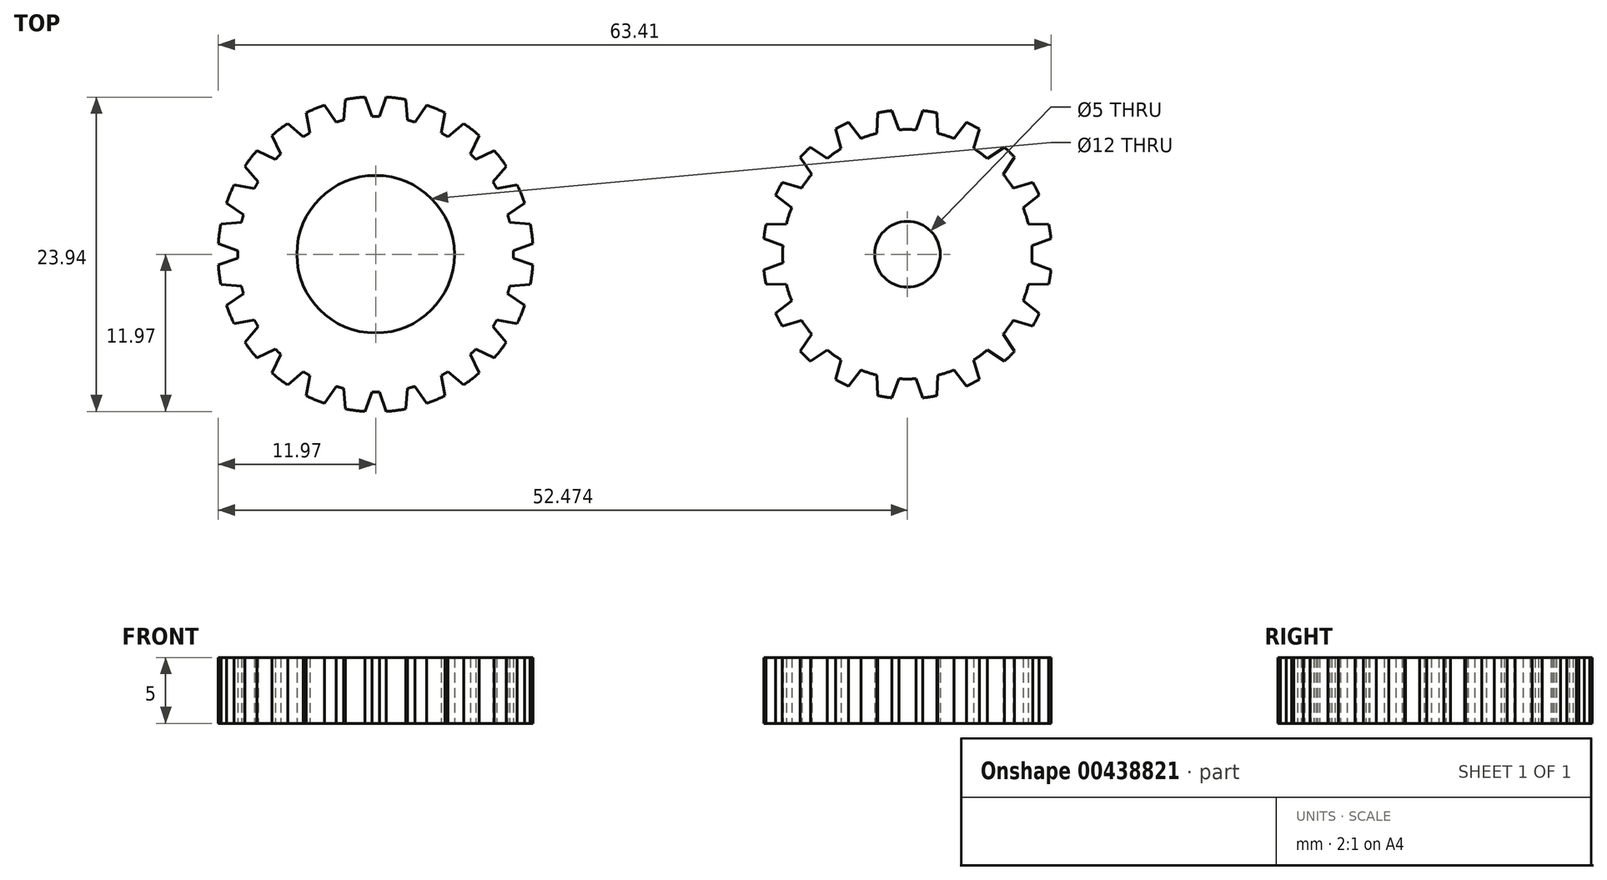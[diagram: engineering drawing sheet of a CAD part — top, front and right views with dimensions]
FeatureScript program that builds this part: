
annotation { "Feature Type Name" : "Feature", "Feature Type Description" : "" }
export const myFeature = defineFeature(function(context is Context, id is Id, definition is map)
    precondition{}
    {
        {
            var Q0;
            Q0=qCreatedBy(makeId("Top.planeOp"),FACE);
            var sketch = newSketch(context, id + "F0", { "sketchPlane" : qUnion([Q0])});
            skCircle(sketch, "E0", {"center": v(0, 0) * mm, "radius": 12 * mm});
            skCircle(sketch, "E1", {"center": v(0, 0) * mm, "radius": 6 * mm});
            skSolve(sketch);
        }
        {
            var Q0;
            Q0 = qSketchRegion(id + "F0", true);
            extrude(context, id + "F1", {"entities" : qUnion([Q0]), "depth" : 5 * mm});
        }
        {
            var Q0;
            Q0=qCreatedBy(makeId("Top.planeOp"),FACE);
            var sketch = newSketch(context, id + "F2", { "sketchPlane" : qUnion([Q0])});
            skArc(sketch, "E2", {"start": v(0.29, 10.5) * mm, "mid": v(0, 10.5) * mm, "end": v(-0.29, 10.5) * mm});
            skLineSegment(sketch, "E3", {"start": v(0.29, 10.5) * mm, "end": v(1.18, 12.95) * mm});
            skLineSegment(sketch, "E4.MirrorCS", {"start": v(-0.29, 10.5) * mm, "end": v(-1.18, 12.95) * mm});
            skLineSegment(sketch, "E5.1.0", {"start": v(-3, 10.06) * mm, "end": v(-4.49, 12.2) * mm});
            skArc(sketch, "E5.1.2", {"start": v(-2.44, 10.21) * mm, "mid": v(-2.72, 10.14) * mm, "end": v(-3, 10.06) * mm});
            skLineSegment(sketch, "E5.1.3", {"start": v(-2.44, 10.21) * mm, "end": v(-2.21, 12.81) * mm});
            skLineSegment(sketch, "E5.2.0", {"start": v(-5.5, 8.95) * mm, "end": v(-7.5, 10.62) * mm});
            skArc(sketch, "E5.2.2", {"start": v(-5, 9.23) * mm, "mid": v(-5.25, 9.1) * mm, "end": v(-5.5, 8.95) * mm});
            skLineSegment(sketch, "E5.2.3", {"start": v(-5, 9.23) * mm, "end": v(-5.45, 11.8) * mm});
            skLineSegment(sketch, "E5.3.0", {"start": v(-7.62, 7.22) * mm, "end": v(-9.99, 8.32) * mm});
            skArc(sketch, "E5.3.2", {"start": v(-7.22, 7.62) * mm, "mid": v(-7.42, 7.42) * mm, "end": v(-7.62, 7.22) * mm});
            skLineSegment(sketch, "E5.3.3", {"start": v(-7.22, 7.62) * mm, "end": v(-8.32, 9.99) * mm});
            skLineSegment(sketch, "E5.4.0", {"start": v(-9.23, 5) * mm, "end": v(-11.8, 5.45) * mm});
            skArc(sketch, "E5.4.2", {"start": v(-8.95, 5.5) * mm, "mid": v(-9.1, 5.25) * mm, "end": v(-9.23, 5) * mm});
            skLineSegment(sketch, "E5.4.3", {"start": v(-8.95, 5.5) * mm, "end": v(-10.62, 7.5) * mm});
            skLineSegment(sketch, "E5.5.0", {"start": v(-10.21, 2.44) * mm, "end": v(-12.81, 2.21) * mm});
            skArc(sketch, "E5.5.2", {"start": v(-10.06, 3) * mm, "mid": v(-10.14, 2.72) * mm, "end": v(-10.21, 2.44) * mm});
            skLineSegment(sketch, "E5.5.3", {"start": v(-10.06, 3) * mm, "end": v(-12.2, 4.49) * mm});
            skLineSegment(sketch, "E5.6.0", {"start": v(-10.5, -0.29) * mm, "end": v(-12.95, -1.18) * mm});
            skArc(sketch, "E5.6.2", {"start": v(-10.5, 0.29) * mm, "mid": v(-10.5, 0) * mm, "end": v(-10.5, -0.29) * mm});
            skLineSegment(sketch, "E5.6.3", {"start": v(-10.5, 0.29) * mm, "end": v(-12.95, 1.18) * mm});
            skLineSegment(sketch, "E5.7.0", {"start": v(-10.06, -3) * mm, "end": v(-12.2, -4.49) * mm});
            skArc(sketch, "E5.7.2", {"start": v(-10.21, -2.44) * mm, "mid": v(-10.14, -2.72) * mm, "end": v(-10.06, -3) * mm});
            skLineSegment(sketch, "E5.7.3", {"start": v(-10.21, -2.44) * mm, "end": v(-12.81, -2.21) * mm});
            skLineSegment(sketch, "E5.8.0", {"start": v(-8.95, -5.5) * mm, "end": v(-10.62, -7.5) * mm});
            skArc(sketch, "E5.8.2", {"start": v(-9.23, -5) * mm, "mid": v(-9.1, -5.25) * mm, "end": v(-8.95, -5.5) * mm});
            skLineSegment(sketch, "E5.8.3", {"start": v(-9.23, -5) * mm, "end": v(-11.8, -5.45) * mm});
            skLineSegment(sketch, "E5.9.0", {"start": v(-7.22, -7.62) * mm, "end": v(-8.32, -9.99) * mm});
            skArc(sketch, "E5.9.2", {"start": v(-7.62, -7.22) * mm, "mid": v(-7.42, -7.42) * mm, "end": v(-7.22, -7.62) * mm});
            skLineSegment(sketch, "E5.9.3", {"start": v(-7.62, -7.22) * mm, "end": v(-9.99, -8.32) * mm});
            skLineSegment(sketch, "E6.1.10.0", {"start": v(-5, -9.23) * mm, "end": v(-5.45, -11.8) * mm});
            skArc(sketch, "E6.7.10.0", {"start": v(-5.5, -8.95) * mm, "mid": v(-5.25, -9.1) * mm, "end": v(-5, -9.23) * mm});
            skLineSegment(sketch, "E6.11.10.0", {"start": v(-5.5, -8.95) * mm, "end": v(-7.5, -10.62) * mm});
            skLineSegment(sketch, "E6.1.11.0", {"start": v(-2.44, -10.21) * mm, "end": v(-2.21, -12.81) * mm});
            skArc(sketch, "E6.7.11.0", {"start": v(-3, -10.06) * mm, "mid": v(-2.72, -10.14) * mm, "end": v(-2.44, -10.21) * mm});
            skLineSegment(sketch, "E6.11.11.0", {"start": v(-3, -10.06) * mm, "end": v(-4.49, -12.2) * mm});
            skLineSegment(sketch, "E6.1.12.0", {"start": v(0.29, -10.5) * mm, "end": v(1.18, -12.95) * mm});
            skArc(sketch, "E6.7.12.0", {"start": v(-0.29, -10.5) * mm, "mid": v(0, -10.5) * mm, "end": v(0.29, -10.5) * mm});
            skLineSegment(sketch, "E6.11.12.0", {"start": v(-0.29, -10.5) * mm, "end": v(-1.18, -12.95) * mm});
            skLineSegment(sketch, "E6.1.13.0", {"start": v(3, -10.06) * mm, "end": v(4.49, -12.2) * mm});
            skArc(sketch, "E6.7.13.0", {"start": v(2.44, -10.21) * mm, "mid": v(2.72, -10.14) * mm, "end": v(3, -10.06) * mm});
            skLineSegment(sketch, "E6.11.13.0", {"start": v(2.44, -10.21) * mm, "end": v(2.21, -12.81) * mm});
            skLineSegment(sketch, "E7.1.14.0", {"start": v(5.5, -8.95) * mm, "end": v(7.5, -10.62) * mm});
            skArc(sketch, "E7.7.14.0", {"start": v(5, -9.23) * mm, "mid": v(5.25, -9.1) * mm, "end": v(5.5, -8.95) * mm});
            skLineSegment(sketch, "E7.11.14.0", {"start": v(5, -9.23) * mm, "end": v(5.45, -11.8) * mm});
            skLineSegment(sketch, "E7.1.15.0", {"start": v(7.62, -7.22) * mm, "end": v(9.99, -8.32) * mm});
            skArc(sketch, "E7.7.15.0", {"start": v(7.22, -7.62) * mm, "mid": v(7.42, -7.42) * mm, "end": v(7.62, -7.22) * mm});
            skLineSegment(sketch, "E7.11.15.0", {"start": v(7.22, -7.62) * mm, "end": v(8.32, -9.99) * mm});
            skLineSegment(sketch, "E7.1.16.0", {"start": v(9.23, -5) * mm, "end": v(11.8, -5.45) * mm});
            skArc(sketch, "E7.7.16.0", {"start": v(8.95, -5.5) * mm, "mid": v(9.1, -5.25) * mm, "end": v(9.23, -5) * mm});
            skLineSegment(sketch, "E7.11.16.0", {"start": v(8.95, -5.5) * mm, "end": v(10.62, -7.5) * mm});
            skLineSegment(sketch, "E7.1.17.0", {"start": v(10.21, -2.44) * mm, "end": v(12.81, -2.21) * mm});
            skArc(sketch, "E7.7.17.0", {"start": v(10.06, -3) * mm, "mid": v(10.14, -2.72) * mm, "end": v(10.21, -2.44) * mm});
            skLineSegment(sketch, "E7.11.17.0", {"start": v(10.06, -3) * mm, "end": v(12.2, -4.49) * mm});
            skLineSegment(sketch, "E7.1.18.0", {"start": v(10.5, 0.29) * mm, "end": v(12.95, 1.18) * mm});
            skArc(sketch, "E7.7.18.0", {"start": v(10.5, -0.29) * mm, "mid": v(10.5, 0) * mm, "end": v(10.5, 0.29) * mm});
            skLineSegment(sketch, "E7.11.18.0", {"start": v(10.5, -0.29) * mm, "end": v(12.95, -1.18) * mm});
            skLineSegment(sketch, "E7.1.19.0", {"start": v(10.06, 3) * mm, "end": v(12.2, 4.49) * mm});
            skArc(sketch, "E7.7.19.0", {"start": v(10.21, 2.44) * mm, "mid": v(10.14, 2.72) * mm, "end": v(10.06, 3) * mm});
            skLineSegment(sketch, "E7.11.19.0", {"start": v(10.21, 2.44) * mm, "end": v(12.81, 2.21) * mm});
            skLineSegment(sketch, "E7.1.20.0", {"start": v(8.95, 5.5) * mm, "end": v(10.62, 7.5) * mm});
            skArc(sketch, "E7.7.20.0", {"start": v(9.23, 5) * mm, "mid": v(9.1, 5.25) * mm, "end": v(8.95, 5.5) * mm});
            skLineSegment(sketch, "E7.11.20.0", {"start": v(9.23, 5) * mm, "end": v(11.8, 5.45) * mm});
            skLineSegment(sketch, "E7.1.21.0", {"start": v(7.22, 7.62) * mm, "end": v(8.32, 9.99) * mm});
            skArc(sketch, "E7.7.21.0", {"start": v(7.62, 7.22) * mm, "mid": v(7.42, 7.42) * mm, "end": v(7.22, 7.62) * mm});
            skLineSegment(sketch, "E7.11.21.0", {"start": v(7.62, 7.22) * mm, "end": v(9.99, 8.32) * mm});
            skLineSegment(sketch, "E7.1.22.0", {"start": v(5, 9.23) * mm, "end": v(5.45, 11.8) * mm});
            skArc(sketch, "E7.7.22.0", {"start": v(5.5, 8.95) * mm, "mid": v(5.25, 9.1) * mm, "end": v(5, 9.23) * mm});
            skLineSegment(sketch, "E7.11.22.0", {"start": v(5.5, 8.95) * mm, "end": v(7.5, 10.62) * mm});
            skLineSegment(sketch, "E7.1.23.0", {"start": v(2.44, 10.21) * mm, "end": v(2.21, 12.81) * mm});
            skArc(sketch, "E7.7.23.0", {"start": v(3, 10.06) * mm, "mid": v(2.72, 10.14) * mm, "end": v(2.44, 10.21) * mm});
            skLineSegment(sketch, "E7.11.23.0", {"start": v(3, 10.06) * mm, "end": v(4.49, 12.2) * mm});
            skCircle(sketch, "E8", {"center": v(0, 0) * mm, "radius": 12 * mm, "construction": true});
            skArc(sketch, "E9", {"start": v(-0.82, 11.97) * mm, "mid": v(0, 12) * mm, "end": v(0.82, 11.97) * mm});
            skArc(sketch, "E10.1.0", {"start": v(-3.9, 11.35) * mm, "mid": v(-3.1, 11.6) * mm, "end": v(-2.3, 11.78) * mm});
            skArc(sketch, "E10.2.0", {"start": v(-6.7, 9.96) * mm, "mid": v(-6, 10.4) * mm, "end": v(-5.27, 10.78) * mm});
            skArc(sketch, "E10.3.0", {"start": v(-9.05, 7.88) * mm, "mid": v(-8.49, 8.49) * mm, "end": v(-7.88, 9.05) * mm});
            skArc(sketch, "E10.4.0", {"start": v(-10.78, 5.27) * mm, "mid": v(-10.4, 6) * mm, "end": v(-9.96, 6.7) * mm});
            skArc(sketch, "E10.5.0", {"start": v(-11.78, 2.3) * mm, "mid": v(-11.6, 3.1) * mm, "end": v(-11.35, 3.9) * mm});
            skArc(sketch, "E10.6.0", {"start": v(-11.97, -0.82) * mm, "mid": v(-12, 0) * mm, "end": v(-11.97, 0.82) * mm});
            skArc(sketch, "E10.7.0", {"start": v(-11.35, -3.9) * mm, "mid": v(-11.6, -3.1) * mm, "end": v(-11.78, -2.3) * mm});
            skArc(sketch, "E10.8.0", {"start": v(-9.96, -6.7) * mm, "mid": v(-10.4, -6) * mm, "end": v(-10.78, -5.27) * mm});
            skArc(sketch, "E10.9.0", {"start": v(-7.88, -9.05) * mm, "mid": v(-8.49, -8.49) * mm, "end": v(-9.05, -7.88) * mm});
            skArc(sketch, "E10.10.0", {"start": v(-5.27, -10.78) * mm, "mid": v(-6, -10.4) * mm, "end": v(-6.7, -9.96) * mm});
            skArc(sketch, "E10.11.0", {"start": v(-2.3, -11.78) * mm, "mid": v(-3.1, -11.6) * mm, "end": v(-3.9, -11.35) * mm});
            skArc(sketch, "E10.12.0", {"start": v(0.82, -11.97) * mm, "mid": v(0, -12) * mm, "end": v(-0.82, -11.97) * mm});
            skArc(sketch, "E10.13.0", {"start": v(3.9, -11.35) * mm, "mid": v(3.1, -11.6) * mm, "end": v(2.3, -11.78) * mm});
            skArc(sketch, "E10.14.0", {"start": v(6.7, -9.96) * mm, "mid": v(6, -10.4) * mm, "end": v(5.27, -10.78) * mm});
            skArc(sketch, "E10.15.0", {"start": v(9.05, -7.88) * mm, "mid": v(8.49, -8.49) * mm, "end": v(7.88, -9.05) * mm});
            skArc(sketch, "E10.16.0", {"start": v(10.78, -5.27) * mm, "mid": v(10.4, -6) * mm, "end": v(9.96, -6.7) * mm});
            skArc(sketch, "E10.17.0", {"start": v(11.78, -2.3) * mm, "mid": v(11.6, -3.1) * mm, "end": v(11.35, -3.9) * mm});
            skArc(sketch, "E10.18.0", {"start": v(11.97, 0.82) * mm, "mid": v(12, 0) * mm, "end": v(11.97, -0.82) * mm});
            skArc(sketch, "E10.19.0", {"start": v(11.35, 3.9) * mm, "mid": v(11.6, 3.1) * mm, "end": v(11.78, 2.3) * mm});
            skArc(sketch, "E10.20.0", {"start": v(9.96, 6.7) * mm, "mid": v(10.4, 6) * mm, "end": v(10.78, 5.27) * mm});
            skArc(sketch, "E10.21.0", {"start": v(7.88, 9.05) * mm, "mid": v(8.49, 8.49) * mm, "end": v(9.05, 7.88) * mm});
            skArc(sketch, "E10.22.0", {"start": v(5.27, 10.78) * mm, "mid": v(6, 10.4) * mm, "end": v(6.7, 9.96) * mm});
            skArc(sketch, "E10.23.0", {"start": v(2.3, 11.78) * mm, "mid": v(3.1, 11.6) * mm, "end": v(3.9, 11.35) * mm});
            skSolve(sketch);
        }
        {
            var Q0;
            Q0 = qSketchRegion(id + "F2", true);
            extrude(context, id + "F3", {"entities" : qUnion([Q0]), "operationType" : NewBodyOperationType.REMOVE, "endBound" : BoundingType.UP_TO_NEXT, "depth" : 25 * mm});
        }
        {
            var Q0;
            Q0=qCreatedBy(makeId("Top.planeOp"),FACE);
            var sketch = newSketch(context, id + "F4", { "sketchPlane" : qUnion([Q0])});
            skCircle(sketch, "E11", {"center": v(40.5, 0) * mm, "radius": 11 * mm});
            skCircle(sketch, "E12", {"center": v(40.5, 0) * mm, "radius": 2.5 * mm});
            skSolve(sketch);
        }
        {
            var Q0;
            Q0 = qSketchRegion(id + "F4", true);
            extrude(context, id + "F5", {"entities" : qUnion([Q0]), "depth" : 5 * mm});
        }
        {
            var Q0;
            Q0=makeQuery(id+"F5.opExtrude","CAP_FACE",FACE,{"disambiguationData":[OSD([sQuery(id+"F4.wireOp",EDGE,"E11")])],"isStart":true});
            var sketch = newSketch(context, id + "F6", { "sketchPlane" : qUnion([Q0])});
            skLineSegment(sketch, "E13", {"start": v(40.5, 0) * mm, "end": v(40.5, -11) * mm, "construction": true});
            skArc(sketch, "E14", {"start": v(39.86, -9.48) * mm, "mid": v(40.5, -9.5) * mm, "end": v(41.15, -9.48) * mm});
            skLineSegment(sketch, "E15", {"start": v(41.15, -9.48) * mm, "end": v(41.68, -10.94) * mm});
            skLineSegment(sketch, "E16.MirrorCS", {"start": v(39.86, -9.48) * mm, "end": v(39.33, -10.94) * mm});
            skArc(sketch, "E17.0", {"start": v(39.33, -10.94) * mm, "mid": v(40.5, -11) * mm, "end": v(41.68, -10.94) * mm});
            skArc(sketch, "E18.1.0", {"start": v(42.82, -9.21) * mm, "mid": v(43.44, -9.04) * mm, "end": v(44.05, -8.81) * mm});
            skLineSegment(sketch, "E18.1.1", {"start": v(44.05, -8.81) * mm, "end": v(45, -10.04) * mm});
            skArc(sketch, "E18.1.2", {"start": v(42.76, -10.77) * mm, "mid": v(43.9, -10.46) * mm, "end": v(45, -10.04) * mm});
            skLineSegment(sketch, "E18.1.3", {"start": v(42.82, -9.21) * mm, "end": v(42.76, -10.77) * mm});
            skArc(sketch, "E18.2.0", {"start": v(45.55, -8.05) * mm, "mid": v(46.09, -7.69) * mm, "end": v(46.6, -7.29) * mm});
            skLineSegment(sketch, "E18.2.1", {"start": v(46.6, -7.29) * mm, "end": v(47.89, -8.16) * mm});
            skArc(sketch, "E18.2.2", {"start": v(45.98, -9.54) * mm, "mid": v(46.97, -8.9) * mm, "end": v(47.89, -8.16) * mm});
            skLineSegment(sketch, "E18.2.3", {"start": v(45.55, -8.05) * mm, "end": v(45.98, -9.54) * mm});
            skArc(sketch, "E18.3.0", {"start": v(47.8, -6.1) * mm, "mid": v(48.19, -5.58) * mm, "end": v(48.55, -5.05) * mm});
            skLineSegment(sketch, "E18.3.1", {"start": v(48.55, -5.05) * mm, "end": v(50.04, -5.48) * mm});
            skArc(sketch, "E18.3.2", {"start": v(48.66, -7.38) * mm, "mid": v(49.4, -6.47) * mm, "end": v(50.04, -5.48) * mm});
            skLineSegment(sketch, "E18.3.3", {"start": v(47.8, -6.1) * mm, "end": v(48.66, -7.38) * mm});
            skArc(sketch, "E18.4.0", {"start": v(49.32, -3.54) * mm, "mid": v(49.54, -2.94) * mm, "end": v(49.72, -2.31) * mm});
            skLineSegment(sketch, "E18.4.1", {"start": v(49.72, -2.31) * mm, "end": v(51.27, -2.26) * mm});
            skArc(sketch, "E18.4.2", {"start": v(50.54, -4.5) * mm, "mid": v(50.97, -3.4) * mm, "end": v(51.27, -2.26) * mm});
            skLineSegment(sketch, "E18.4.3", {"start": v(49.32, -3.54) * mm, "end": v(50.54, -4.5) * mm});
            skArc(sketch, "E18.5.0", {"start": v(49.98, -0.65) * mm, "mid": v(50, 0) * mm, "end": v(49.98, 0.65) * mm});
            skLineSegment(sketch, "E18.5.1", {"start": v(49.98, 0.65) * mm, "end": v(51.44, 1.18) * mm});
            skArc(sketch, "E18.5.2", {"start": v(51.44, -1.18) * mm, "mid": v(51.5, 0) * mm, "end": v(51.44, 1.18) * mm});
            skLineSegment(sketch, "E18.5.3", {"start": v(49.98, -0.65) * mm, "end": v(51.44, -1.18) * mm});
            skArc(sketch, "E18.6.0", {"start": v(49.72, 2.31) * mm, "mid": v(49.54, 2.94) * mm, "end": v(49.32, 3.54) * mm});
            skLineSegment(sketch, "E18.6.1", {"start": v(49.32, 3.54) * mm, "end": v(50.54, 4.5) * mm});
            skArc(sketch, "E18.6.2", {"start": v(51.27, 2.26) * mm, "mid": v(50.97, 3.4) * mm, "end": v(50.54, 4.5) * mm});
            skLineSegment(sketch, "E18.6.3", {"start": v(49.72, 2.31) * mm, "end": v(51.27, 2.26) * mm});
            skArc(sketch, "E18.7.0", {"start": v(48.55, 5.05) * mm, "mid": v(48.19, 5.58) * mm, "end": v(47.8, 6.1) * mm});
            skLineSegment(sketch, "E18.7.1", {"start": v(47.8, 6.1) * mm, "end": v(48.66, 7.38) * mm});
            skArc(sketch, "E18.7.2", {"start": v(50.04, 5.48) * mm, "mid": v(49.4, 6.47) * mm, "end": v(48.66, 7.38) * mm});
            skLineSegment(sketch, "E18.7.3", {"start": v(48.55, 5.05) * mm, "end": v(50.04, 5.48) * mm});
            skArc(sketch, "E18.8.0", {"start": v(46.6, 7.29) * mm, "mid": v(46.09, 7.69) * mm, "end": v(45.55, 8.05) * mm});
            skLineSegment(sketch, "E18.8.1", {"start": v(45.55, 8.05) * mm, "end": v(45.98, 9.54) * mm});
            skArc(sketch, "E18.8.2", {"start": v(47.89, 8.16) * mm, "mid": v(46.97, 8.9) * mm, "end": v(45.98, 9.54) * mm});
            skLineSegment(sketch, "E18.8.3", {"start": v(46.6, 7.29) * mm, "end": v(47.89, 8.16) * mm});
            skArc(sketch, "E18.9.0", {"start": v(44.05, 8.81) * mm, "mid": v(43.44, 9.04) * mm, "end": v(42.82, 9.21) * mm});
            skLineSegment(sketch, "E18.9.1", {"start": v(42.82, 9.21) * mm, "end": v(42.76, 10.77) * mm});
            skArc(sketch, "E18.9.2", {"start": v(45, 10.04) * mm, "mid": v(43.9, 10.46) * mm, "end": v(42.76, 10.77) * mm});
            skLineSegment(sketch, "E18.9.3", {"start": v(44.05, 8.81) * mm, "end": v(45, 10.04) * mm});
            skArc(sketch, "E19.2.10.0", {"start": v(41.15, 9.48) * mm, "mid": v(40.5, 9.5) * mm, "end": v(39.86, 9.48) * mm});
            skLineSegment(sketch, "E19.4.10.0", {"start": v(39.86, 9.48) * mm, "end": v(39.33, 10.94) * mm});
            skArc(sketch, "E19.7.10.0", {"start": v(41.68, 10.94) * mm, "mid": v(40.5, 11) * mm, "end": v(39.33, 10.94) * mm});
            skLineSegment(sketch, "E19.11.10.0", {"start": v(41.15, 9.48) * mm, "end": v(41.68, 10.94) * mm});
            skArc(sketch, "E19.2.11.0", {"start": v(38.2, 9.21) * mm, "mid": v(37.57, 9.04) * mm, "end": v(36.96, 8.81) * mm});
            skLineSegment(sketch, "E19.4.11.0", {"start": v(36.96, 8.81) * mm, "end": v(36, 10.04) * mm});
            skArc(sketch, "E19.7.11.0", {"start": v(38.25, 10.77) * mm, "mid": v(37.1, 10.46) * mm, "end": v(36, 10.04) * mm});
            skLineSegment(sketch, "E19.11.11.0", {"start": v(38.2, 9.21) * mm, "end": v(38.25, 10.77) * mm});
            skArc(sketch, "E19.2.12.0", {"start": v(35.46, 8.05) * mm, "mid": v(34.92, 7.69) * mm, "end": v(34.4, 7.29) * mm});
            skLineSegment(sketch, "E19.4.12.0", {"start": v(34.4, 7.29) * mm, "end": v(33.12, 8.16) * mm});
            skArc(sketch, "E19.7.12.0", {"start": v(35.03, 9.54) * mm, "mid": v(34.04, 8.9) * mm, "end": v(33.12, 8.16) * mm});
            skLineSegment(sketch, "E19.11.12.0", {"start": v(35.46, 8.05) * mm, "end": v(35.03, 9.54) * mm});
            skArc(sketch, "E19.2.13.0", {"start": v(33.22, 6.1) * mm, "mid": v(32.82, 5.58) * mm, "end": v(32.46, 5.05) * mm});
            skLineSegment(sketch, "E19.4.13.0", {"start": v(32.46, 5.05) * mm, "end": v(30.96, 5.48) * mm});
            skArc(sketch, "E19.7.13.0", {"start": v(32.35, 7.38) * mm, "mid": v(31.6, 6.47) * mm, "end": v(30.96, 5.48) * mm});
            skLineSegment(sketch, "E19.11.13.0", {"start": v(33.22, 6.1) * mm, "end": v(32.35, 7.38) * mm});
            skArc(sketch, "E19.2.14.0", {"start": v(31.7, 3.54) * mm, "mid": v(31.47, 2.94) * mm, "end": v(31.3, 2.31) * mm});
            skLineSegment(sketch, "E19.4.14.0", {"start": v(31.3, 2.31) * mm, "end": v(29.74, 2.26) * mm});
            skArc(sketch, "E19.7.14.0", {"start": v(30.47, 4.5) * mm, "mid": v(30.04, 3.4) * mm, "end": v(29.74, 2.26) * mm});
            skLineSegment(sketch, "E19.11.14.0", {"start": v(31.7, 3.54) * mm, "end": v(30.47, 4.5) * mm});
            skArc(sketch, "E19.2.15.0", {"start": v(31.03, 0.65) * mm, "mid": v(31, 0) * mm, "end": v(31.03, -0.65) * mm});
            skLineSegment(sketch, "E19.4.15.0", {"start": v(31.03, -0.65) * mm, "end": v(29.57, -1.18) * mm});
            skArc(sketch, "E19.7.15.0", {"start": v(29.57, 1.18) * mm, "mid": v(29.5, 0) * mm, "end": v(29.57, -1.18) * mm});
            skLineSegment(sketch, "E19.11.15.0", {"start": v(31.03, 0.65) * mm, "end": v(29.57, 1.18) * mm});
            skArc(sketch, "E19.2.16.0", {"start": v(31.3, -2.31) * mm, "mid": v(31.47, -2.94) * mm, "end": v(31.7, -3.54) * mm});
            skLineSegment(sketch, "E19.4.16.0", {"start": v(31.7, -3.54) * mm, "end": v(30.47, -4.5) * mm});
            skArc(sketch, "E19.7.16.0", {"start": v(29.74, -2.26) * mm, "mid": v(30.04, -3.4) * mm, "end": v(30.47, -4.5) * mm});
            skLineSegment(sketch, "E19.11.16.0", {"start": v(31.3, -2.31) * mm, "end": v(29.74, -2.26) * mm});
            skArc(sketch, "E19.2.17.0", {"start": v(32.46, -5.05) * mm, "mid": v(32.82, -5.58) * mm, "end": v(33.22, -6.1) * mm});
            skLineSegment(sketch, "E19.4.17.0", {"start": v(33.22, -6.1) * mm, "end": v(32.35, -7.38) * mm});
            skArc(sketch, "E19.7.17.0", {"start": v(30.96, -5.48) * mm, "mid": v(31.6, -6.47) * mm, "end": v(32.35, -7.38) * mm});
            skLineSegment(sketch, "E19.11.17.0", {"start": v(32.46, -5.05) * mm, "end": v(30.96, -5.48) * mm});
            skArc(sketch, "E19.2.18.0", {"start": v(34.4, -7.29) * mm, "mid": v(34.92, -7.69) * mm, "end": v(35.46, -8.05) * mm});
            skLineSegment(sketch, "E19.4.18.0", {"start": v(35.46, -8.05) * mm, "end": v(35.03, -9.54) * mm});
            skArc(sketch, "E19.7.18.0", {"start": v(33.12, -8.16) * mm, "mid": v(34.04, -8.9) * mm, "end": v(35.03, -9.54) * mm});
            skLineSegment(sketch, "E19.11.18.0", {"start": v(34.4, -7.29) * mm, "end": v(33.12, -8.16) * mm});
            skArc(sketch, "E19.2.19.0", {"start": v(36.96, -8.81) * mm, "mid": v(37.57, -9.04) * mm, "end": v(38.2, -9.21) * mm});
            skLineSegment(sketch, "E19.4.19.0", {"start": v(38.2, -9.21) * mm, "end": v(38.25, -10.77) * mm});
            skArc(sketch, "E19.7.19.0", {"start": v(36, -10.04) * mm, "mid": v(37.1, -10.46) * mm, "end": v(38.25, -10.77) * mm});
            skLineSegment(sketch, "E19.11.19.0", {"start": v(36.96, -8.81) * mm, "end": v(36, -10.04) * mm});
            skSolve(sketch);
        }
        {
            var Q0;
            Q0 = qSketchRegion(id + "F6", true);
            extrude(context, id + "F7", {"entities" : qUnion([Q0]), "operationType" : NewBodyOperationType.REMOVE, "endBound" : BoundingType.UP_TO_NEXT, "oppositeDirection" : true, "depth" : 25 * mm});
        }
    });
